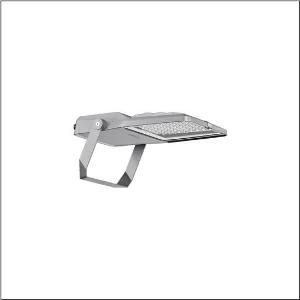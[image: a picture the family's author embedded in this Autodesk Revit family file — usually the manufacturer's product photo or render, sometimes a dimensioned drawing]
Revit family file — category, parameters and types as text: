
# Revit family: floodlight_fl_21_iq_mini___pl64_5xa7772c3e1a_c8ef
name_source: partatom
category: Lighting Fixtures
units: mm (PartAtom-declared; Revit-internal decimal feet)

## family parameters
Cut with Voids When Loaded = No
Host = Face
Light Source = No
Part Type = Normal
Room Calculation Point = No
Round Connector Dimension = Use Diameter
Shared = No

## types (1)
- --- (1 x LED, 10150 lm, 87.2 W, 3000K)
    Apparent Load = 87 VA
    CIE Flux Codes = 28 80 98 100 100
    Color Rendering = 80
    Color Temperature = 3000K
    Default Elevation = 1800 mm
    Description = Floodlight FL 21 iQ mini, floodlight, primary light control with lens, of PMMA, primary optical cover: protective disc, of toughened safety glass, transparent, light distribution: PL64, light emission: direct distribution, installation type: surface-mounted, lamps: LED, High Power LED, rated values: 10.150lm | 87,2W | 116,4lm/W (begin service life); end service life: 10.150lm | 92,1W; at 50% lumin. flux: 5.075lm | 40,1W | 126,6lm/W, colour temperature: 3000K, colour rendering: CRI > 80, light colour: 830, light setting 1 begin service life: 100% | 10.150lm | 87,2W | 116,4lm/W | 3.000K, light setting 1 end service life: 92,1W, further light settings possible, control: Street-Remote, Auto-Match, Temp-Guard, Night-Set, Smart-Wire, Desk-Remote (wireless, voltage-free reading and setting of iQ features in the workshop via application-optimized NFC function/RFID function), optimised constant luminous flux control (CLO 2.0), pre-setting: linear dimming characteristic, with terminal, 6-pole, mains connection: 220..240V, AC, 50/60Hz, luminaire housing, of diecast aluminium, powder-coated, SITECO metallic grey (DB 702S), corrosivity category C5 mid according to DIN EN ISO 12944suitable for swimming poolschlorine-resistant, sealing non-destructively replaceable, mounting bracket, of steel, galvanised, powder-coated, SITECO metallic grey (DB 702S), protection rating (complete): IP66, insulation class (complete): insulation class II (safety insulation), certification: CE, ENEC, VDE, protection symbol: D, impact resistance: IK08, permissible operating ambient temperature: -40..+40°C, permissible operating ambient temperature for outdoor applications: -40..+50°C, standard: DIN EN 12944, LABS conformity tested according to VDMA 24364:2018-05, packaging unit: 1 piece

Light Distribution: PL64
    Height = 70 mm
    Lamp = 1 x LED
    Lamp Light Flux = 10150 lm
    Lamp Power = 87.2 W
    Lamp count = 1
    Length = 485 mm
    Luminous efficacy = 116 lm/W
    Manufacturer = Siteco
    ModVariant = No
    Model = 5XA7772C3E1A
    Mounting Place = Pole
    Mounting Type = Pole annexe
    Number of Poles = 1
    OnlyDefault = Yes
    Power Factor = 1
    Product Name = Floodlight FL 21 iQ mini | PL64
    Product group = floodlight | pylon annexe
    ProductGroupID = 6201
    Protection Class = Protection class II
    Protection Degree = IP 66
    RLX_Detail_Level = 1
    RLX_Emergency_Light_Flux = 0 lm
    RLX_Emergency_Type = 0
    RLX_Emergency_Type_DB = No
    RlxData = <blob elided: 96661 chars, md5=bc9b5d6a>
    Socket = socket
    Standby Power = 0 W
    System Light Flux = 10150 lm
    System Power = 87 W
    Type Comments = factory setting: luminous flux: 100 % | dim-lin: 254 | 456 mA
    Type Image = l_1006845.jpg
    URL = http://relux.com
    VarID = @adj_167359
    Voltage = 0 V
    Weight = 0.00 kg
    Width = 337 mm

## geometry (parser evidence)
native form markers: Blend x4, Sweep x12
no freeform markers — native parametric forms only
